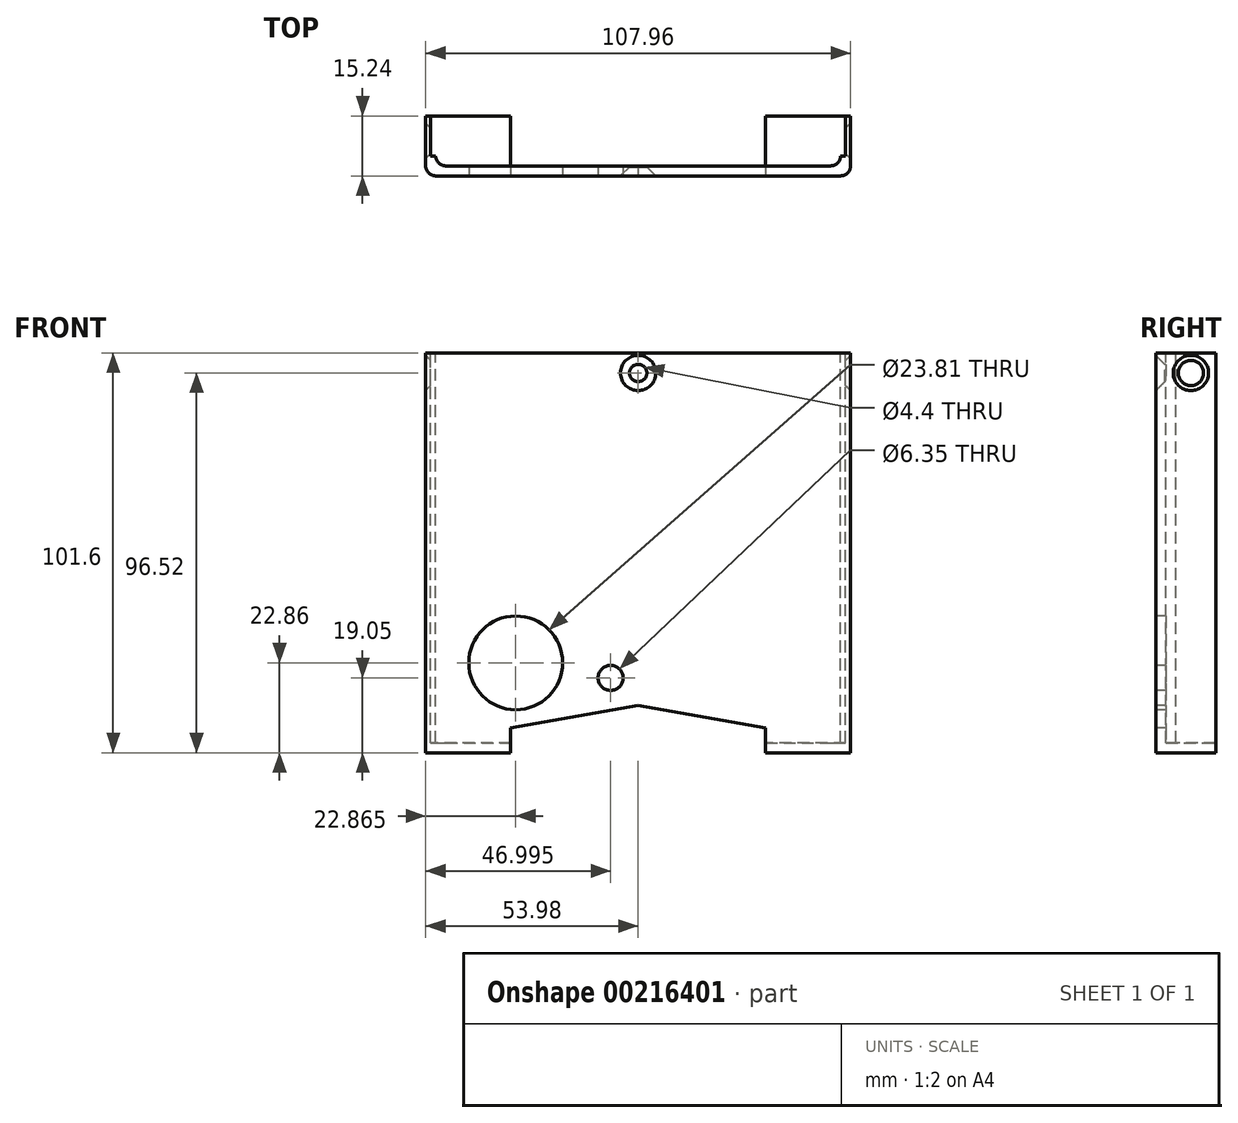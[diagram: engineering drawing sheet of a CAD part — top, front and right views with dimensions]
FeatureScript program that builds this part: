
annotation { "Feature Type Name" : "Feature", "Feature Type Description" : "" }
export const myFeature = defineFeature(function(context is Context, id is Id, definition is map)
    precondition{}
    {
        {
            var Q0;
            Q0=qCreatedBy(makeId("Top.planeOp"),FACE);
            var sketch = newSketch(context, id + "F0", { "sketchPlane" : qUnion([Q0])});
            skLineSegment(sketch, "E0", {"start": v(-53.98, 0) * mm, "end": v(53.98, 0) * mm});
            skLineSegment(sketch, "E1", {"start": v(53.98, 0) * mm, "end": v(53.98, 15.24) * mm});
            skLineSegment(sketch, "E2", {"start": v(53.97, 15.24) * mm, "end": v(-53.97, 15.24) * mm});
            skLineSegment(sketch, "E3", {"start": v(-53.98, 15.24) * mm, "end": v(-53.98, 0) * mm});
            skPoint(sketch, "E4", {"position": v(0, 0) * mm});
            skSolve(sketch);
        }
        {
            var Q0;
            Q0 = qSketchRegion(id + "F0", true);
            extrude(context, id + "F1", {"entities" : qUnion([Q0]), "depth" : 101.6 * mm});
        }
        {
            var Q0;
            Q0=makeQuery(id+"F1.opExtrude","SWEPT_EDGE",EDGE,{"disambiguationData":[OSD([sQuery(id+"F0.wireOp",EDGE,"E0"),sQuery(id+"F0.wireOp",EDGE,"E1")])]});
            var Q1;
            Q1=makeQuery(id+"F1.opExtrude","SWEPT_EDGE",EDGE,{"disambiguationData":[OSD([sQuery(id+"F0.wireOp",EDGE,"E0"),sQuery(id+"F0.wireOp",EDGE,"E3")])]});
            fillet(context, id + "F2", {"entities" : qUnion([Q0, Q1]), "radius" : 2.54 * mm, "tangentPropagation" : true, "allowEdgeOverflow" : false});
        }
        {
            var Q0;
            Q0=makeQuery(id+"F1.opExtrude","CAP_FACE",FACE,{"disambiguationData":[OSD([sQuery(id+"F0.wireOp",EDGE,"E0"),sQuery(id+"F0.wireOp",EDGE,"E1"),sQuery(id+"F0.wireOp",EDGE,"E2"),sQuery(id+"F0.wireOp",EDGE,"E3")])],"isStart":false});
            var Q1;
            Q1=makeQuery(id+"Fi8aWM1QPLw7Rl5_1.boolean.opBoolean","COPY",FACE,{"derivedFrom":makeQuery(id+"Fi8aWM1QPLw7Rl5_1.opExtrude","SWEPT_FACE",FACE,{"disambiguationData":[OSD([sQuery(id+"FJr2nPUcqSUhdGq_1.wireOp",EDGE,"bkIaCIVR-jec4-OExd-qZ9r-p5tLa0SBglyw")])]})});
            shell(context, id + "F3", {"entities" : qUnion([Q0, Q1]), "thickness" : 2.54 * mm});
        }
        {
            var Q0;
            Q0=makeQuery(id+"F1.opExtrude","SWEPT_FACE",FACE,{"disambiguationData":[OSD([sQuery(id+"F0.wireOp",EDGE,"E0")])]});
            var sketch = newSketch(context, id + "F4", { "sketchPlane" : qUnion([Q0])});
            skLineSegment(sketch, "E5", {"start": v(0, 12.06) * mm, "end": v(-83.59, -2.68) * mm});
            skLineSegment(sketch, "E6", {"start": v(-83.59, -2.68) * mm, "end": v(83.59, -2.68) * mm});
            skLineSegment(sketch, "E7", {"start": v(83.59, -2.68) * mm, "end": v(0, 12.06) * mm});
            skLineSegment(sketch, "E8", {"start": v(-32.38, 0) * mm, "end": v(32.39, 0) * mm});
            skLineSegment(sketch, "E9", {"start": v(32.39, 0) * mm, "end": v(32.39, 6.35) * mm});
            skLineSegment(sketch, "E10", {"start": v(-32.38, 0) * mm, "end": v(-32.38, 6.35) * mm});
            skCircle(sketch, "E11", {"center": v(-31.12, 22.86) * mm, "radius": 11.9 * mm});
            skSolve(sketch);
        }
        {
            var Q0;
            Q0=makeQuery(id+"F4.imprint","IMPRINT",FACE,{"disambiguationData":[TD([[makeQuery(id+"F4.imprint","IMPRINT",EDGE,{"derivedFrom":sQuery(id+"F4.wireOp",EDGE,"E8")}),1.0]])]});
            var Q1;
            Q1=makeQuery(id+"F4.imprint","IMPRINT",FACE,{"disambiguationData":[TD([[makeQuery(id+"F4.imprint","IMPRINT",EDGE,{"derivedFrom":sQuery(id+"F4.wireOp",EDGE,"E11")}),1.0]])]});
            extrude(context, id + "F5", {"entities" : qUnion([Q0, Q1]), "operationType" : NewBodyOperationType.REMOVE, "oppositeDirection" : true, "depth" : 25.4 * mm});
        }
        {
            var Q0;
            Q0=makeQuery(id+"F3.opShell","OFFSET_EDGE",EDGE,{"disambiguationData":[OSD([sQuery(id+"F0.wireOp",EDGE,"E0"),sQuery(id+"F0.wireOp",EDGE,"E3")])]});
            var Q1;
            Q1=makeQuery(id+"F3.opShell","OFFSET_EDGE",EDGE,{"disambiguationData":[OSD([sQuery(id+"F0.wireOp",EDGE,"E0"),sQuery(id+"F0.wireOp",EDGE,"E1")])]});
            fillet(context, id + "F6", {"entities" : qUnion([Q0, Q1]), "radius" : 2.54 * mm, "tangentPropagation" : true, "allowEdgeOverflow" : false});
        }
        {
            var Q0;
            Q0=makeQuery(id+"F1.opExtrude","CAP_FACE",FACE,{"disambiguationData":[OSD([sQuery(id+"F0.wireOp",EDGE,"E0"),sQuery(id+"F0.wireOp",EDGE,"E1"),sQuery(id+"F0.wireOp",EDGE,"E2"),sQuery(id+"F0.wireOp",EDGE,"E3")])],"isStart":false});
            var sketch = newSketch(context, id + "F7", { "sketchPlane" : qUnion([Q0])});
            skLineSegment(sketch, "E12.bottom", {"start": v(52.7, 5.08) * mm, "end": v(-52.7, 5.08) * mm});
            skLineSegment(sketch, "E12.top", {"start": v(52.7, 43.74) * mm, "end": v(-52.7, 43.74) * mm});
            skLineSegment(sketch, "E12.left", {"start": v(52.7, 5.08) * mm, "end": v(52.7, 43.74) * mm});
            skLineSegment(sketch, "E12.right", {"start": v(-52.7, 5.08) * mm, "end": v(-52.7, 43.74) * mm});
            skSolve(sketch);
        }
        {
            var Q0;
            Q0 = qSketchRegion(id + "F7", true);
            var Q1;
            {var subQ0=sQuery(id+"F0.wireOp",EDGE,"E0");var subQ1=sQuery(id+"F0.wireOp",EDGE,"E1");Q1=makeQuery(id+"F5.boolean.opBoolean","SPLIT",FACE,{"disambiguationData":[TD([makeQuery(id+"F3.opShell","OFFSET_FACE",FACE,{"disambiguationData":[OSD([subQ1])]})])],"derivedFrom":makeQuery(id+"F3.opShell","OFFSET_FACE",FACE,{"disambiguationData":[OSD([subQ0,subQ1,sQuery(id+"F0.wireOp",EDGE,"E2"),sQuery(id+"F0.wireOp",EDGE,"E3")])]})});}
            extrude(context, id + "F8", {"entities" : qUnion([Q0]), "operationType" : NewBodyOperationType.REMOVE, "endBound" : BoundingType.UP_TO_SURFACE, "oppositeDirection" : true, "endBoundEntityFace" : qUnion([Q1]), "depth" : 84.33 * mm});
        }
        {
            var Q0;
            Q0=makeQuery(id+"F1.opExtrude","SWEPT_FACE",FACE,{"disambiguationData":[OSD([sQuery(id+"F0.wireOp",EDGE,"E0")])]});
            var sketch = newSketch(context, id + "F9", { "sketchPlane" : qUnion([Q0])});
            skPoint(sketch, "E13", {"position": v(0, 96.52) * mm});
            skSolve(sketch);
        }
        {
            var Q0;
            Q0=sQuery(id+"F9.wireOp",VERTEX,"E13");
            var Q1;
            Q1=makeQuery(id+"F1.opExtrude","SWEPT_BODY",BODY,{"disambiguationData":[OSD([sQuery(id+"F0.wireOp",EDGE,"E0"),sQuery(id+"F0.wireOp",EDGE,"E1"),sQuery(id+"F0.wireOp",EDGE,"E2"),sQuery(id+"F0.wireOp",EDGE,"E3")])]});
            hole(context, id + "F10", {"style" : HoleStyle.C_SINK, "endStyle" : HoleEndStyle.BLIND, "standardTappedOrClearance" : lookupTablePath({ "standard" : "ISO", "fit" : "Normal", "size" : "M4", "type" : "Clearance" }), "standardBlindInLast" : lookupTablePath({ "fit" : "Standard", "standard" : "ISO", "size" : "M4", "type" : "Clearance" }), "holeDiameter" : 4.4 * mm, "cSinkDiameter" : 8.96 * mm, "cSinkAngle" : 90 * degree, "holeDepth" : 37.19 * mm, "tappedDepth" : 34.94 * mm, "tapClearance" : 3, "locations" : qUnion([Q0]), "scope" : qUnion([Q1])});
        }
        {
            var Q0;
            Q0=makeQuery(id+"F1.opExtrude","SWEPT_FACE",FACE,{"disambiguationData":[OSD([sQuery(id+"F0.wireOp",EDGE,"E3")])]});
            var sketch = newSketch(context, id + "F11", { "sketchPlane" : qUnion([Q0])});
            skPoint(sketch, "E14", {"position": v(-8.9, 96.52) * mm});
            skSolve(sketch);
        }
        {
            var Q0;
            Q0=makeQuery(id+"F1.opExtrude","SWEPT_FACE",FACE,{"disambiguationData":[OSD([sQuery(id+"F0.wireOp",EDGE,"E1")])]});
            var sketch = newSketch(context, id + "F12", { "sketchPlane" : qUnion([Q0])});
            skPoint(sketch, "E15", {"position": v(8.9, 96.52) * mm});
            skSolve(sketch);
        }
        {
            var Q0;
            Q0=sQuery(id+"F12.wireOp",VERTEX,"E15");
            var Q1;
            Q1=sQuery(id+"F11.wireOp",VERTEX,"E14");
            var Q2;
            Q2=makeQuery(id+"F1.opExtrude","SWEPT_BODY",BODY,{"disambiguationData":[OSD([sQuery(id+"F0.wireOp",EDGE,"E0"),sQuery(id+"F0.wireOp",EDGE,"E1"),sQuery(id+"F0.wireOp",EDGE,"E2"),sQuery(id+"F0.wireOp",EDGE,"E3")])]});
            hole(context, id + "F13", {"style" : HoleStyle.C_SINK, "endStyle" : HoleEndStyle.BLIND, "standardTappedOrClearance" : lookupTablePath({ "standard" : "ISO", "fit" : "Normal", "size" : "M4", "type" : "Clearance" }), "standardBlindInLast" : lookupTablePath({ "fit" : "Standard", "standard" : "ISO", "size" : "M4", "type" : "Clearance" }), "holeDiameter" : 4.4 * mm, "cSinkDiameter" : 8.96 * mm, "cSinkAngle" : 90 * degree, "holeDepth" : 37.19 * mm, "tappedDepth" : 34.92 * mm, "tapClearance" : 3, "locations" : qUnion([Q0, Q1]), "scope" : qUnion([Q2])});
        }
        {
            var Q0;
            Q0=makeQuery(id+"F1.opExtrude","SWEPT_FACE",FACE,{"disambiguationData":[OSD([sQuery(id+"F0.wireOp",EDGE,"E0")])]});
            var sketch = newSketch(context, id + "F14", { "sketchPlane" : qUnion([Q0])});
            skCircle(sketch, "E16", {"center": v(-6.98, 19.05) * mm, "radius": 3.18 * mm});
            skSolve(sketch);
        }
        {
            var Q0;
            Q0 = qSketchRegion(id + "F14", true);
            extrude(context, id + "F15", {"entities" : qUnion([Q0]), "operationType" : NewBodyOperationType.REMOVE, "oppositeDirection" : true, "depth" : 25.4 * mm});
        }
    });
